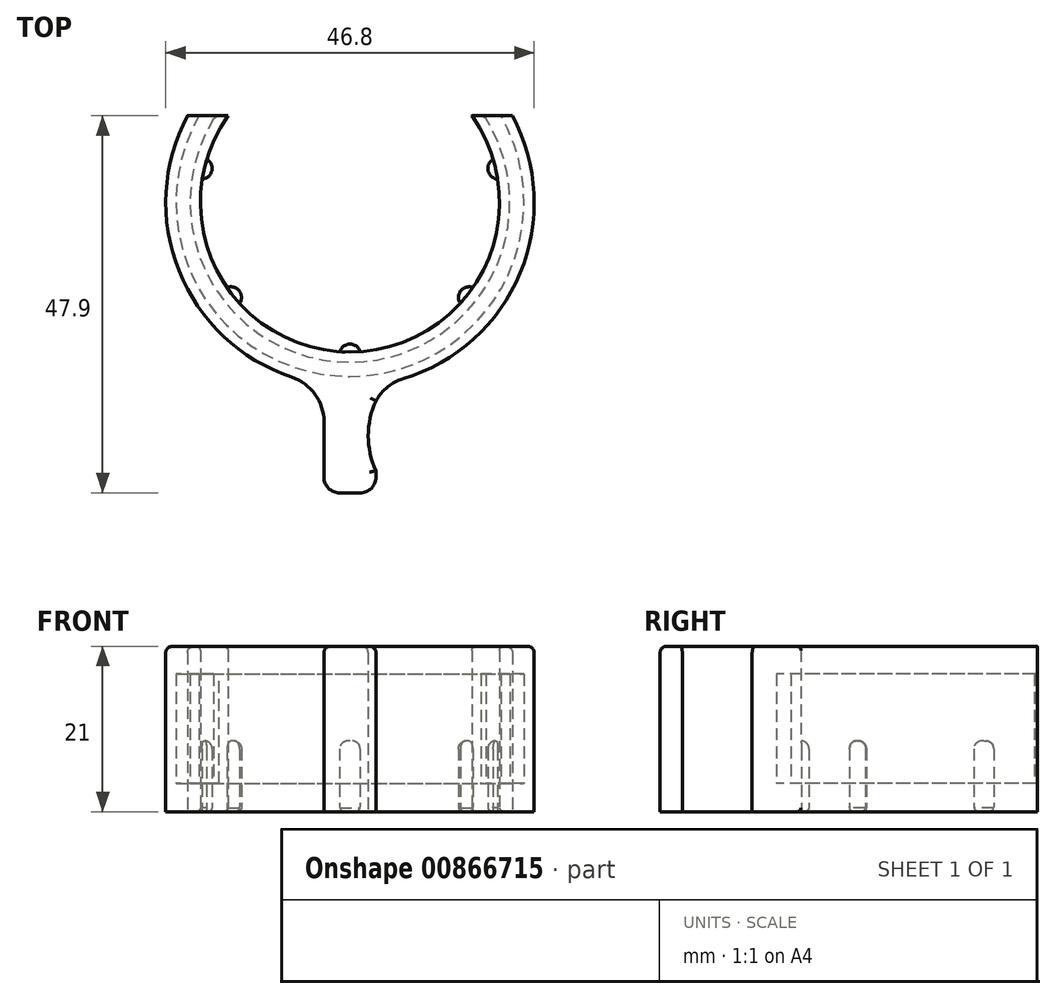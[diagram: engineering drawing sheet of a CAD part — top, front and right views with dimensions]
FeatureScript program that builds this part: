
annotation { "Feature Type Name" : "Feature", "Feature Type Description" : "" }
export const myFeature = defineFeature(function(context is Context, id is Id, definition is map)
    precondition{}
    {
        {
            var Q0;
            Q0=qCreatedBy(makeId("Top.planeOp"),FACE);
            var sketch = newSketch(context, id + "F0", { "sketchPlane" : qUnion([Q0])});
            skLineSegment(sketch, "E0", {"start": v(-35.75, 0) * mm, "end": v(38.1, 0) * mm, "construction": true});
            skLineSegment(sketch, "E1", {"start": v(0, -25.74) * mm, "end": v(0, 33.72) * mm, "construction": true});
            skArc(sketch, "E2", {"start": v(-15.5, 11) * mm, "mid": v(0, -19) * mm, "end": v(15.5, 11) * mm});
            skArc(sketch, "E3.0", {"start": v(-20.65, 11) * mm, "mid": v(0, -23.4) * mm, "end": v(20.65, 11) * mm});
            skLineSegment(sketch, "E4", {"start": v(0, 0) * mm, "end": v(0, 11) * mm, "construction": true});
            skLineSegment(sketch, "E5", {"start": v(-39.56, 11) * mm, "end": v(58.92, 11) * mm, "construction": true});
            skLineSegment(sketch, "E6", {"start": v(-20.65, 11) * mm, "end": v(-15.5, 11) * mm});
            skLineSegment(sketch, "E7", {"start": v(15.5, 11) * mm, "end": v(20.65, 11) * mm});
            skLineSegment(sketch, "E8", {"start": v(0, -22.4) * mm, "end": v(-3.3, -22.4) * mm});
            skLineSegment(sketch, "E9", {"start": v(-3.3, -22.4) * mm, "end": v(-3.3, -36.9) * mm});
            skLineSegment(sketch, "E10", {"start": v(-3.3, -36.9) * mm, "end": v(0, -36.9) * mm});
            skLineSegment(sketch, "E11", {"start": v(0, -27.35) * mm, "end": v(0, -19.35) * mm});
            skLineSegment(sketch, "E12", {"start": v(0, -22.4) * mm, "end": v(3.3, -22.4) * mm});
            skLineSegment(sketch, "E13", {"start": v(3.3, -22.4) * mm, "end": v(3.3, -25.2) * mm});
            skLineSegment(sketch, "E14", {"start": v(3.3, -36.9) * mm, "end": v(0, -36.9) * mm});
            skArc(sketch, "E15", {"start": v(1.3, -18.96) * mm, "mid": v(0, -18) * mm, "end": v(-1.3, -18.96) * mm});
            skArc(sketch, "E16.1.0", {"start": v(15.63, -10.8) * mm, "mid": v(14.07, -11.22) * mm, "end": v(14.02, -12.83) * mm});
            skArc(sketch, "E16.2.0", {"start": v(18.2, 5.48) * mm, "mid": v(17.55, 4) * mm, "end": v(18.77, 2.96) * mm});
            skArc(sketch, "E16.5.0", {"start": v(-18.77, 2.96) * mm, "mid": v(-17.55, 4) * mm, "end": v(-18.2, 5.48) * mm});
            skArc(sketch, "E16.6.0", {"start": v(-14.02, -12.83) * mm, "mid": v(-14.07, -11.22) * mm, "end": v(-15.63, -10.8) * mm});
            skPoint(sketch, "E17.centerSnap0", {"position": v(3.3, -29.65) * mm});
            skArc(sketch, "E18.trimOffspring", {"start": v(3.3, -25.2) * mm, "mid": v(2.32, -29.65) * mm, "end": v(3.3, -34.1) * mm});
            skPoint(sketch, "E17.center.orphan", {"position": v(9.55, -29.65) * mm});
            skLineSegment(sketch, "E19.trimOffspring", {"start": v(3.3, -34.1) * mm, "end": v(3.3, -36.9) * mm});
            skSolve(sketch);
        }
        {
            var Q0;
            Q0=qCreatedBy(makeId("Top.planeOp"),FACE);
            var sketch = newSketch(context, id + "F1", { "sketchPlane" : qUnion([Q0])});
            skLineSegment(sketch, "E20", {"start": v(-36.32, 6.56) * mm, "end": v(37.53, 6.56) * mm, "construction": true});
            skLineSegment(sketch, "E21", {"start": v(0, -20.3) * mm, "end": v(0, 33.42) * mm, "construction": true});
            skLineSegment(sketch, "E22", {"start": v(0, -0.3) * mm, "end": v(0, 11.7) * mm, "construction": true});
            skLineSegment(sketch, "E23", {"start": v(-39.56, 11.7) * mm, "end": v(58.92, 11.7) * mm, "construction": true});
            skLineSegment(sketch, "E24", {"start": v(-19.86, 11.7) * mm, "end": v(-14.73, 11.7) * mm});
            skLineSegment(sketch, "E25", {"start": v(14.73, 11.7) * mm, "end": v(19.86, 11.7) * mm});
            skArc(sketch, "E26.0", {"start": v(-15.74, 12.82) * mm, "mid": v(0, -20.3) * mm, "end": v(15.74, 12.82) * mm});
            skArc(sketch, "E27.0", {"start": v(-17.13, 13.96) * mm, "mid": v(0, -22.1) * mm, "end": v(17.13, 13.96) * mm});
            skLineSegment(sketch, "E28", {"start": v(-17.13, 13.96) * mm, "end": v(-15.74, 12.82) * mm});
            skLineSegment(sketch, "E29", {"start": v(15.74, 12.82) * mm, "end": v(17.13, 13.96) * mm});
            skSolve(sketch);
        }
        {
            var Q0;
            {var subQ0=sQuery(id+"F0.wireOp",EDGE,"E10");Q0=makeQuery(id+"F0.imprint","IMPRINT",FACE,{"disambiguationData":[TD([[makeQuery(id+"F0.imprint","IMPRINT",EDGE,{"derivedFrom":subQ0}),1.0]])]});}
            var Q1;
            {var subQ5=sQuery(id+"F0.wireOp",EDGE,"E8");Q1=makeQuery(id+"F0.imprint","IMPRINT",FACE,{"disambiguationData":[TD([[makeQuery(id+"F0.imprint","IMPRINT",EDGE,{"derivedFrom":subQ5}),1.0]])]});}
            var Q2;
            {var subQ5=sQuery(id+"F0.wireOp",EDGE,"E12");Q2=makeQuery(id+"F0.imprint","IMPRINT",FACE,{"disambiguationData":[TD([[makeQuery(id+"F0.imprint","IMPRINT",EDGE,{"derivedFrom":subQ5}),-1.0]])]});}
            var Q3;
            {var subQ12=sQuery(id+"F0.wireOp",EDGE,"E6");Q3=makeQuery(id+"F0.imprint","IMPRINT",FACE,{"disambiguationData":[TD([[makeQuery(id+"F0.imprint","IMPRINT",EDGE,{"derivedFrom":subQ12}),-1.0]])]});}
            extrude(context, id + "F2", {"entities" : qUnion([Q0, Q1, Q2, Q3]), "depth" : 21 * mm, "offsetDistance" : 25 * mm});
        }
        {
            var Q0;
            Q0=makeQuery(id+"F2.opExtrude","SWEPT_EDGE",EDGE,{"disambiguationData":[OSD([sQuery(id+"F0.wireOp",EDGE,"E3.0"),sQuery(id+"F0.wireOp",EDGE,"E13")])]});
            var Q1;
            Q1=makeQuery(id+"F2.opExtrude","SWEPT_EDGE",EDGE,{"disambiguationData":[OSD([sQuery(id+"F0.wireOp",EDGE,"E3.0"),sQuery(id+"F0.wireOp",EDGE,"E9")])]});
            fillet(context, id + "F3", {"entities" : qUnion([Q0, Q1]), "radius" : 6 * mm, "tangentPropagation" : true, "allowEdgeOverflow" : false});
        }
        {
            var Q0;
            Q0=makeQuery(id+"F2.opExtrude","SWEPT_EDGE",EDGE,{"disambiguationData":[OSD([sQuery(id+"F0.wireOp",EDGE,"E13"),sQuery(id+"F0.wireOp",EDGE,"E14")])]});
            var Q1;
            Q1=makeQuery(id+"F2.opExtrude","SWEPT_EDGE",EDGE,{"disambiguationData":[OSD([sQuery(id+"F0.wireOp",EDGE,"E9"),sQuery(id+"F0.wireOp",EDGE,"E10")])]});
            fillet(context, id + "F4", {"entities" : qUnion([Q0, Q1]), "radius" : 2 * mm, "tangentPropagation" : true, "allowEdgeOverflow" : false});
        }
        {
            var Q0;
            Q0=qSketchRegion(id+"F1",true);
            extrude(context, id + "F5", {"entities" : qUnion([Q0]), "operationType" : NewBodyOperationType.REMOVE, "depth" : 17.5 * mm, "offsetDistance" : 25 * mm, "hasSecondDirection" : true, "secondDirectionOppositeDirection" : false, "secondDirectionDepth" : 3.6 * mm});
        }
        {
            var Q0;
            {var subQ0=sQuery(id+"F0.wireOp",EDGE,"E3.0");Q0=makeQuery(id+"F2.opExtrude","CAP_EDGE",EDGE,{"disambiguationData":[OSD([subQ0]),TDD([makeQuery(id+"F0.imprint","IMPRINT",EDGE,{"disambiguationData":[TD([[makeQuery(id+"F0.imprint","INTERSECT",VERTEX,{"derivedFrom":[subQ0,sQuery(id+"F0.wireOp",EDGE,"E6")]}),-1.0]])],"derivedFrom":subQ0})])],"isStart":false});}
            var Q1;
            Q1=makeQuery(id+"F2.opExtrude","CAP_EDGE",EDGE,{"disambiguationData":[OSD([sQuery(id+"F0.wireOp",EDGE,"E18.trimOffspring")])],"isStart":false});
            var Q2;
            {var subQ0=sQuery(id+"F0.wireOp",EDGE,"E3.0");Q2=makeQuery(id+"F2.opExtrude","CAP_EDGE",EDGE,{"disambiguationData":[OSD([subQ0]),TDD([makeQuery(id+"F0.imprint","IMPRINT",EDGE,{"disambiguationData":[TD([[makeQuery(id+"F0.imprint","INTERSECT",VERTEX,{"derivedFrom":[subQ0,sQuery(id+"F0.wireOp",EDGE,"E7")]}),1.0]])],"derivedFrom":subQ0})])],"isStart":false});}
            fillet(context, id + "F6", {"entities" : qUnion([Q0, Q1, Q2]), "radius" : .8 * mm, "tangentPropagation" : true, "allowEdgeOverflow" : false});
        }
        {
            var Q0;
            Q0=makeQuery(id+"F5.boolean.opBoolean","INTERSECT",EDGE,{"derivedFrom":[makeQuery(id+"F2.opExtrude","SWEPT_FACE",FACE,{"disambiguationData":[OSD([sQuery(id+"F0.wireOp",EDGE,"E6")])]}),makeQuery(id+"F5.opExtrude","SWEPT_FACE",FACE,{"disambiguationData":[OSD([sQuery(id+"F1.wireOp",EDGE,"E26.0")])]})]});
            var Q1;
            Q1=makeQuery(id+"F5.boolean.opBoolean","INTERSECT",EDGE,{"derivedFrom":[makeQuery(id+"F2.opExtrude","SWEPT_FACE",FACE,{"disambiguationData":[OSD([sQuery(id+"F0.wireOp",EDGE,"E7")])]}),makeQuery(id+"F5.opExtrude","SWEPT_FACE",FACE,{"disambiguationData":[OSD([sQuery(id+"F1.wireOp",EDGE,"E26.0")])]})]});
            chamfer(context, id + "F7", {"entities" : qUnion([Q0, Q1]), "width" : .8 * mm, "tangentPropagation" : true});
        }
        {
            var Q0;
            Q0=makeQuery(id+"F2.opExtrude","CAP_EDGE",EDGE,{"disambiguationData":[OSD([sQuery(id+"F0.wireOp",EDGE,"E2")])],"isStart":false});
            var Q1;
            Q1=makeQuery(id+"F2.opExtrude","CAP_EDGE",EDGE,{"disambiguationData":[OSD([sQuery(id+"F0.wireOp",EDGE,"E2")])],"isStart":true});
            fillet(context, id + "F8", {"entities" : qUnion([Q0, Q1]), "radius" : .5 * mm, "tangentPropagation" : true, "allowEdgeOverflow" : false});
        }
        {
            var Q0;
            {var subQ0=sQuery(id+"F0.wireOp",EDGE,"E16.5.0");Q0=makeQuery(id+"F0.imprint","IMPRINT",FACE,{"disambiguationData":[TD([[makeQuery(id+"F0.imprint","IMPRINT",EDGE,{"derivedFrom":subQ0}),1.0]])]});}
            var Q1;
            {var subQ0=sQuery(id+"F0.wireOp",EDGE,"E16.6.0");Q1=makeQuery(id+"F0.imprint","IMPRINT",FACE,{"disambiguationData":[TD([[makeQuery(id+"F0.imprint","IMPRINT",EDGE,{"derivedFrom":subQ0}),1.0]])]});}
            var Q2;
            {var subQ0=sQuery(id+"F0.wireOp",EDGE,"E15");Q2=makeQuery(id+"F0.imprint","IMPRINT",FACE,{"disambiguationData":[TD([[makeQuery(id+"F0.imprint","IMPRINT",EDGE,{"derivedFrom":subQ0}),1.0]])]});}
            var Q3;
            {var subQ0=sQuery(id+"F0.wireOp",EDGE,"E16.1.0");Q3=makeQuery(id+"F0.imprint","IMPRINT",FACE,{"disambiguationData":[TD([[makeQuery(id+"F0.imprint","IMPRINT",EDGE,{"derivedFrom":subQ0}),1.0]])]});}
            var Q4;
            {var subQ0=sQuery(id+"F0.wireOp",EDGE,"E16.2.0");Q4=makeQuery(id+"F0.imprint","IMPRINT",FACE,{"disambiguationData":[TD([[makeQuery(id+"F0.imprint","IMPRINT",EDGE,{"derivedFrom":subQ0}),1.0]])]});}
            extrude(context, id + "F9", {"entities" : qUnion([Q0, Q1, Q2, Q3, Q4]), "operationType" : NewBodyOperationType.ADD, "depth" : 9 * mm, "offsetDistance" : 25 * mm});
        }
        {
            var Q0;
            Q0=makeQuery(id+"F9.opExtrude","CAP_EDGE",EDGE,{"disambiguationData":[OSD([sQuery(id+"F0.wireOp",EDGE,"E16.6.0")])],"isStart":false});
            var Q1;
            Q1=makeQuery(id+"F9.opExtrude","CAP_EDGE",EDGE,{"disambiguationData":[OSD([sQuery(id+"F0.wireOp",EDGE,"E15")])],"isStart":false});
            var Q2;
            Q2=makeQuery(id+"F9.opExtrude","CAP_EDGE",EDGE,{"disambiguationData":[OSD([sQuery(id+"F0.wireOp",EDGE,"E16.5.0")])],"isStart":false});
            var Q3;
            Q3=makeQuery(id+"F9.opExtrude","CAP_EDGE",EDGE,{"disambiguationData":[OSD([sQuery(id+"F0.wireOp",EDGE,"E16.1.0")])],"isStart":false});
            var Q4;
            Q4=makeQuery(id+"F9.opExtrude","CAP_EDGE",EDGE,{"disambiguationData":[OSD([sQuery(id+"F0.wireOp",EDGE,"E16.2.0")])],"isStart":false});
            fillet(context, id + "F10", {"entities" : qUnion([Q0, Q1, Q2, Q3, Q4]), "radius" : 1 * mm, "tangentPropagation" : true, "allowEdgeOverflow" : false});
        }
        {
            var Q0;
            Q0=makeQuery(id+"F9.opExtrude","CAP_EDGE",EDGE,{"disambiguationData":[OSD([sQuery(id+"F0.wireOp",EDGE,"E15")])],"isStart":true});
            var Q1;
            Q1=makeQuery(id+"F9.opExtrude","CAP_EDGE",EDGE,{"disambiguationData":[OSD([sQuery(id+"F0.wireOp",EDGE,"E16.6.0")])],"isStart":true});
            var Q2;
            Q2=makeQuery(id+"F9.opExtrude","CAP_EDGE",EDGE,{"disambiguationData":[OSD([sQuery(id+"F0.wireOp",EDGE,"E16.5.0")])],"isStart":true});
            var Q3;
            Q3=makeQuery(id+"F9.opExtrude","CAP_EDGE",EDGE,{"disambiguationData":[OSD([sQuery(id+"F0.wireOp",EDGE,"E16.1.0")])],"isStart":true});
            var Q4;
            Q4=makeQuery(id+"F9.opExtrude","CAP_EDGE",EDGE,{"disambiguationData":[OSD([sQuery(id+"F0.wireOp",EDGE,"E16.2.0")])],"isStart":true});
            fillet(context, id + "F11", {"entities" : qUnion([Q0, Q1, Q2, Q3, Q4]), "radius" : .6 * mm, "tangentPropagation" : true, "allowEdgeOverflow" : false});
        }
    });
